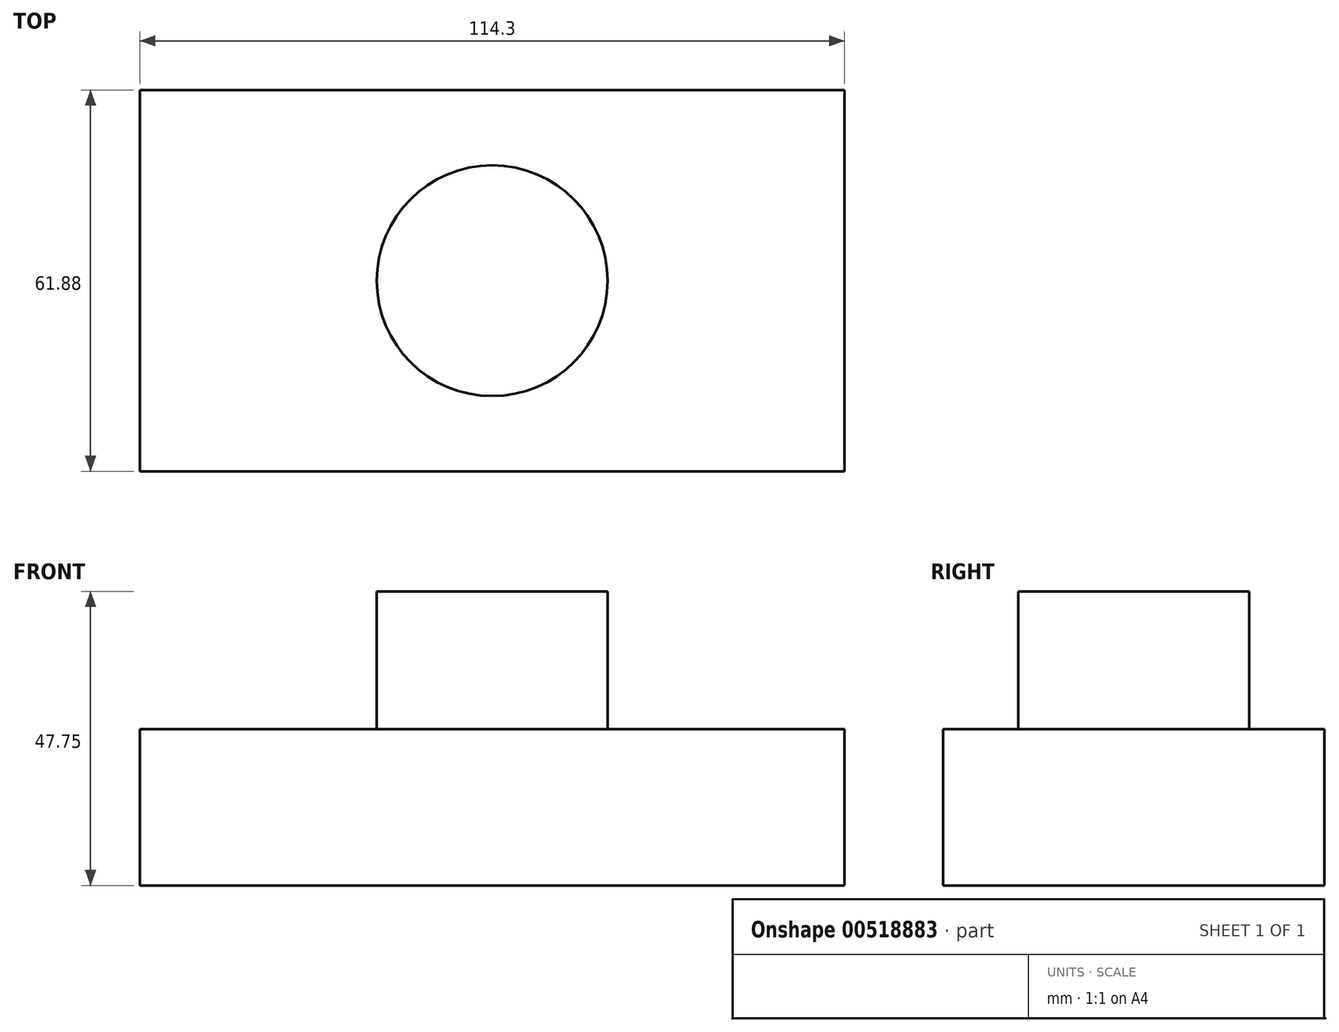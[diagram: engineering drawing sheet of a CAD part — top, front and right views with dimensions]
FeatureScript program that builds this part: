
annotation { "Feature Type Name" : "Feature", "Feature Type Description" : "" }
export const myFeature = defineFeature(function(context is Context, id is Id, definition is map)
    precondition{}
    {
        {
            var Q0;
            Q0=qCreatedBy(makeId("Top.planeOp"),FACE);
            var sketch = newSketch(context, id + "F0", { "sketchPlane" : qUnion([Q0])});
            skLineSegment(sketch, "E0.bottom", {"start": v(57.15, 30.94) * mm, "end": v(-57.15, 30.94) * mm});
            skLineSegment(sketch, "E0.top", {"start": v(57.15, -30.94) * mm, "end": v(-57.15, -30.94) * mm});
            skLineSegment(sketch, "E0.left", {"start": v(57.15, 30.94) * mm, "end": v(57.15, -30.94) * mm});
            skLineSegment(sketch, "E0.right", {"start": v(-57.15, 30.94) * mm, "end": v(-57.15, -30.94) * mm});
            skPoint(sketch, "E0.middle", {"position": v(0, 0) * mm});
            skCircle(sketch, "E1", {"center": v(0, 0) * mm, "radius": 18.72 * mm});
            skSolve(sketch);
        }
        {
            var Q0;
            Q0=makeQuery(id+"F0.imprint","IMPRINT",FACE,{"disambiguationData":[TD([[makeQuery(id+"F0.imprint","IMPRINT",EDGE,{"derivedFrom":sQuery(id+"F0.wireOp",EDGE,"E0.bottom")}),1.0]])]});
            var sketch = newSketch(context, id + "F1", { "sketchPlane" : qUnion([Q0])});
            skSolve(sketch);
        }
        {
            var Q0;
            Q0=makeQuery(id+"F0.imprint","IMPRINT",FACE,{"disambiguationData":[TD([[makeQuery(id+"F0.imprint","IMPRINT",EDGE,{"derivedFrom":sQuery(id+"F0.wireOp",EDGE,"E0.bottom")}),1.0]])]});
            extrude(context, id + "F2", {"entities" : qUnion([Q0]), "depth" : 25.4 * mm});
        }
        {
            var Q0;
            Q0=makeQuery(id+"F1.imprint","IMPRINT",FACE,{"disambiguationData":[TD([[makeQuery(id+"F1.imprint","IMPRINT",EDGE,{"derivedFrom":makeQuery(id+"F0.imprint","IMPRINT",EDGE,{"derivedFrom":sQuery(id+"F0.wireOp",EDGE,"E1")})}),1.0]])]});
            extrude(context, id + "F3", {"entities" : qUnion([Q0]), "operationType" : NewBodyOperationType.ADD, "depth" : 47.75 * mm});
        }
    });
